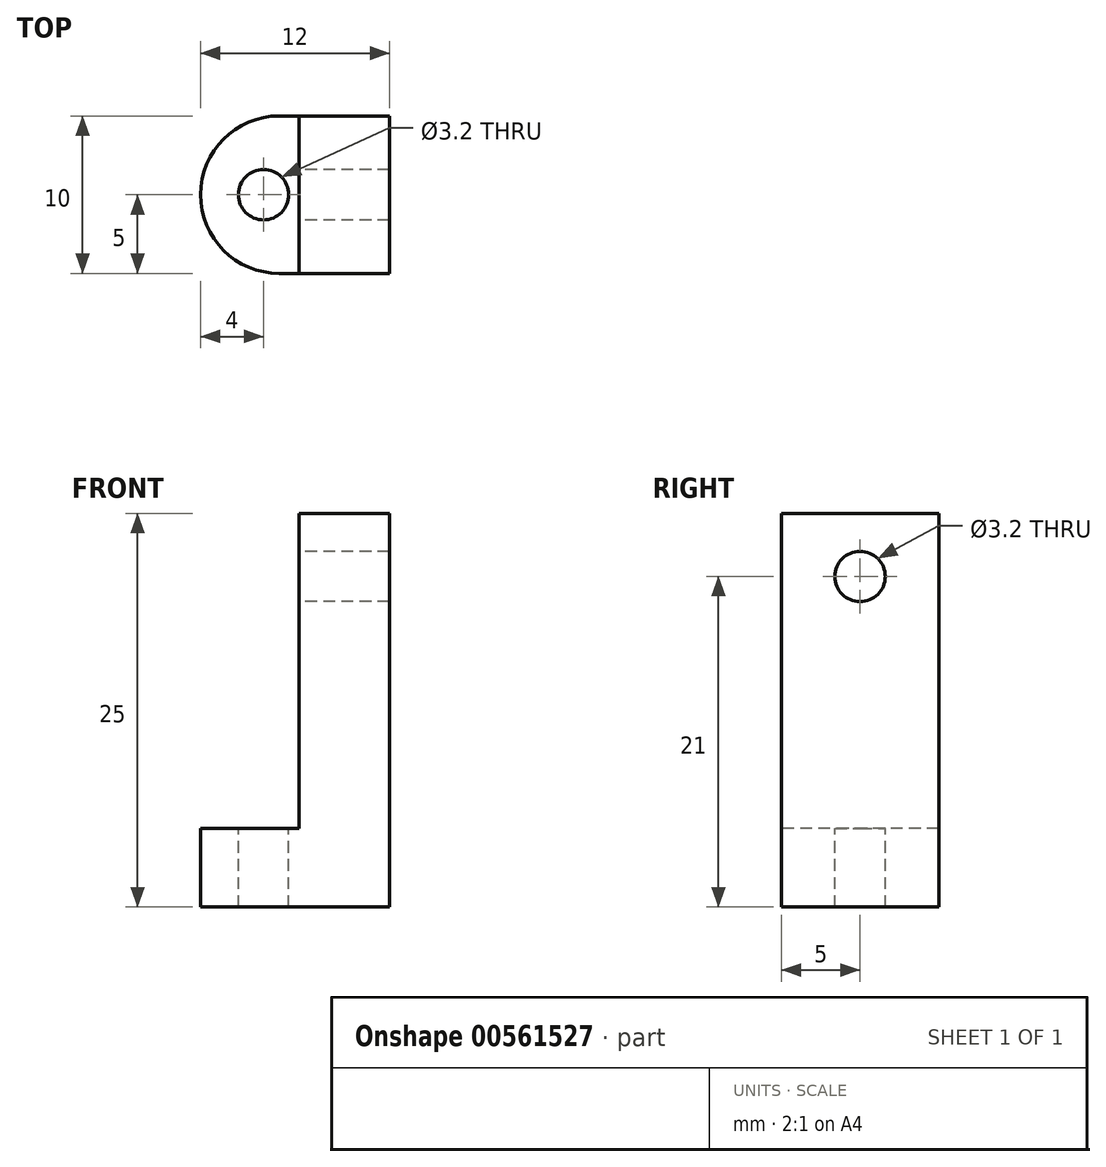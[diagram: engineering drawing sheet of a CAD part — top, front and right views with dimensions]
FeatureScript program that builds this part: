
annotation { "Feature Type Name" : "Feature", "Feature Type Description" : "" }
export const myFeature = defineFeature(function(context is Context, id is Id, definition is map)
    precondition{}
    {
        {
            var Q0;
            Q0=qCreatedBy(makeId("Top.planeOp"),FACE);
            var sketch = newSketch(context, id + "F0", { "sketchPlane" : qUnion([Q0])});
            skLineSegment(sketch, "E0.bottom", {"start": v(6, 5) * mm, "end": v(-6, 5) * mm});
            skLineSegment(sketch, "E0.top", {"start": v(6, -5) * mm, "end": v(-6, -5) * mm});
            skLineSegment(sketch, "E0.left", {"start": v(6, 5) * mm, "end": v(6, -5) * mm});
            skLineSegment(sketch, "E0.right", {"start": v(-6, 5) * mm, "end": v(-6, -5) * mm});
            skPoint(sketch, "E0.middle", {"position": v(0, 0) * mm});
            skSolve(sketch);
        }
        {
            var Q0;
            Q0 = qSketchRegion(id + "F0", true);
            extrude(context, id + "F1", {"entities" : qUnion([Q0]), "depth" : 5 * mm, "offsetDistance" : 25 * mm});
        }
        {
            var Q0;
            Q0=makeQuery(id+"F1.opExtrude","CAP_FACE",FACE,{"disambiguationData":[OSD([sQuery(id+"F0.wireOp",EDGE,"E0.bottom"),sQuery(id+"F0.wireOp",EDGE,"E0.top"),sQuery(id+"F0.wireOp",EDGE,"E0.left"),sQuery(id+"F0.wireOp",EDGE,"E0.right")])],"isStart":false});
            var sketch = newSketch(context, id + "F2", { "sketchPlane" : qUnion([Q0])});
            skLineSegment(sketch, "E1.bottom", {"start": v(6, 5) * mm, "end": v(0.27, 5) * mm});
            skLineSegment(sketch, "E1.top", {"start": v(6, -5) * mm, "end": v(0.27, -5) * mm});
            skLineSegment(sketch, "E1.left", {"start": v(6, 5) * mm, "end": v(6, -5) * mm});
            skLineSegment(sketch, "E1.right", {"start": v(0.27, 5) * mm, "end": v(0.27, -5) * mm});
            skPoint(sketch, "E1.middle", {"position": v(3.13, 0) * mm});
            skSolve(sketch);
        }
        {
            var Q0;
            Q0 = qSketchRegion(id + "F2", true);
            extrude(context, id + "F3", {"entities" : qUnion([Q0]), "operationType" : NewBodyOperationType.ADD, "depth" : 20 * mm, "offsetDistance" : 25 * mm});
        }
        {
            var Q0;
            Q0=makeQuery(id+"F3.opExtrude","SWEPT_FACE",FACE,{"disambiguationData":[OSD([sQuery(id+"F2.wireOp",EDGE,"E1.right")])]});
            var sketch = newSketch(context, id + "F4", { "sketchPlane" : qUnion([Q0])});
            skCircle(sketch, "E2", {"center": v(0, 21) * mm, "radius": 1.6 * mm});
            skSolve(sketch);
        }
        {
            var Q0;
            Q0 = qSketchRegion(id + "F4", true);
            extrude(context, id + "F5", {"entities" : qUnion([Q0]), "operationType" : NewBodyOperationType.REMOVE, "oppositeDirection" : true, "depth" : 10 * mm, "offsetDistance" : 25 * mm});
        }
        {
            var Q0;
            Q0=makeQuery(id+"F1.opExtrude","CAP_FACE",FACE,{"disambiguationData":[OSD([sQuery(id+"F0.wireOp",EDGE,"E0.bottom"),sQuery(id+"F0.wireOp",EDGE,"E0.top"),sQuery(id+"F0.wireOp",EDGE,"E0.left"),sQuery(id+"F0.wireOp",EDGE,"E0.right")])],"isStart":false});
            var sketch = newSketch(context, id + "F6", { "sketchPlane" : qUnion([Q0])});
            skCircle(sketch, "E3", {"center": v(-2, 0) * mm, "radius": 1.6 * mm});
            skSolve(sketch);
        }
        {
            var Q0;
            Q0 = qSketchRegion(id + "F6", true);
            extrude(context, id + "F7", {"entities" : qUnion([Q0]), "operationType" : NewBodyOperationType.REMOVE, "oppositeDirection" : true, "depth" : 10 * mm, "offsetDistance" : 25 * mm});
        }
        {
            var Q0;
            Q0=makeQuery(id+"F1.opExtrude","SWEPT_EDGE",EDGE,{"disambiguationData":[OSD([sQuery(id+"F0.wireOp",EDGE,"E0.top"),sQuery(id+"F0.wireOp",EDGE,"E0.right")])]});
            var Q1;
            Q1=makeQuery(id+"F1.opExtrude","SWEPT_EDGE",EDGE,{"disambiguationData":[OSD([sQuery(id+"F0.wireOp",EDGE,"E0.bottom"),sQuery(id+"F0.wireOp",EDGE,"E0.right")])]});
            fillet(context, id + "F8", {"entities" : qUnion([Q0, Q1]), "radius" : 5 * mm, "tangentPropagation" : true, "allowEdgeOverflow" : false});
        }
    });
